# Revit family: Edo exist_window dbl-hung 1-unit v2012dan
name_source: partatom
category: Windows
revit_build: Autodesk Revit Architecture 2012 (Build: 20110916_2132(x64)
units: mm (PartAtom-declared; Revit-internal decimal feet)

## types (5) — shared parameters
Assembly Code = B2020100
Description = x
Keynote = 08500.WD
Manufacturer = x
Model = x
Wall Closure = By host
default sash height yN = Yes
frame exterior = 08550 windows- existing
frame interior = 08100 interior trim- white
glass = Glass
grill width = 3/4"
grille lower yN = Yes
grille spaces_vert lower = 3
grille upper yN = Yes
shutter color = 08550 window shutter solid- existing
trim depth- exterior = 2"
trim exterior = 08550 windows- existing
trim interior = 08100 interior trim- white
trim width- interior = 4"
upper sash height = 2' - 0"

## per-type parameters (varying)
| type | Height | Width | ext cap trim yN | ext face offset | grille spaces_horiz | grille spaces_vert upper | shutter face offset | shutter side offset | shutterW | trim width- exterior |
| exist 3-4 x 5-6 | 5' - 7 1/2" | 3' - 5 1/2" | No | 4" | 4 | 3 | 1" | 3" | 1' - 7" | 4" |
| exist 3-0 x 3-6 | 3' - 7 1/2" | 3' - 1 1/2" | Yes | 1" | 4 | 2 | 2" | 0" | 1' - 5" | 5" |
| exist 2-6 x 4-0 dormer | 4' - 1 1/2" | 2' - 7 1/2" | No | 1" | 3 | 2 | 2" | 0" | 1' - 5" | 2" |
| exist 2-6 x 4-0 | 4' - 1 1/2" | 2' - 7 1/2" | Yes | 1" | 3 | 2 | 2" | 0" | 1' - 5" | 5" |
| exist 3-0 x 4-6 bay window | 4' - 7 1/2" | 3' - 1 1/2" | No | 1" | 3 | 2 | 2" | 0" | 1' - 5" | 5" |

## geometry (parser evidence)
native form markers: Sweep x15
no freeform markers — native parametric forms only
